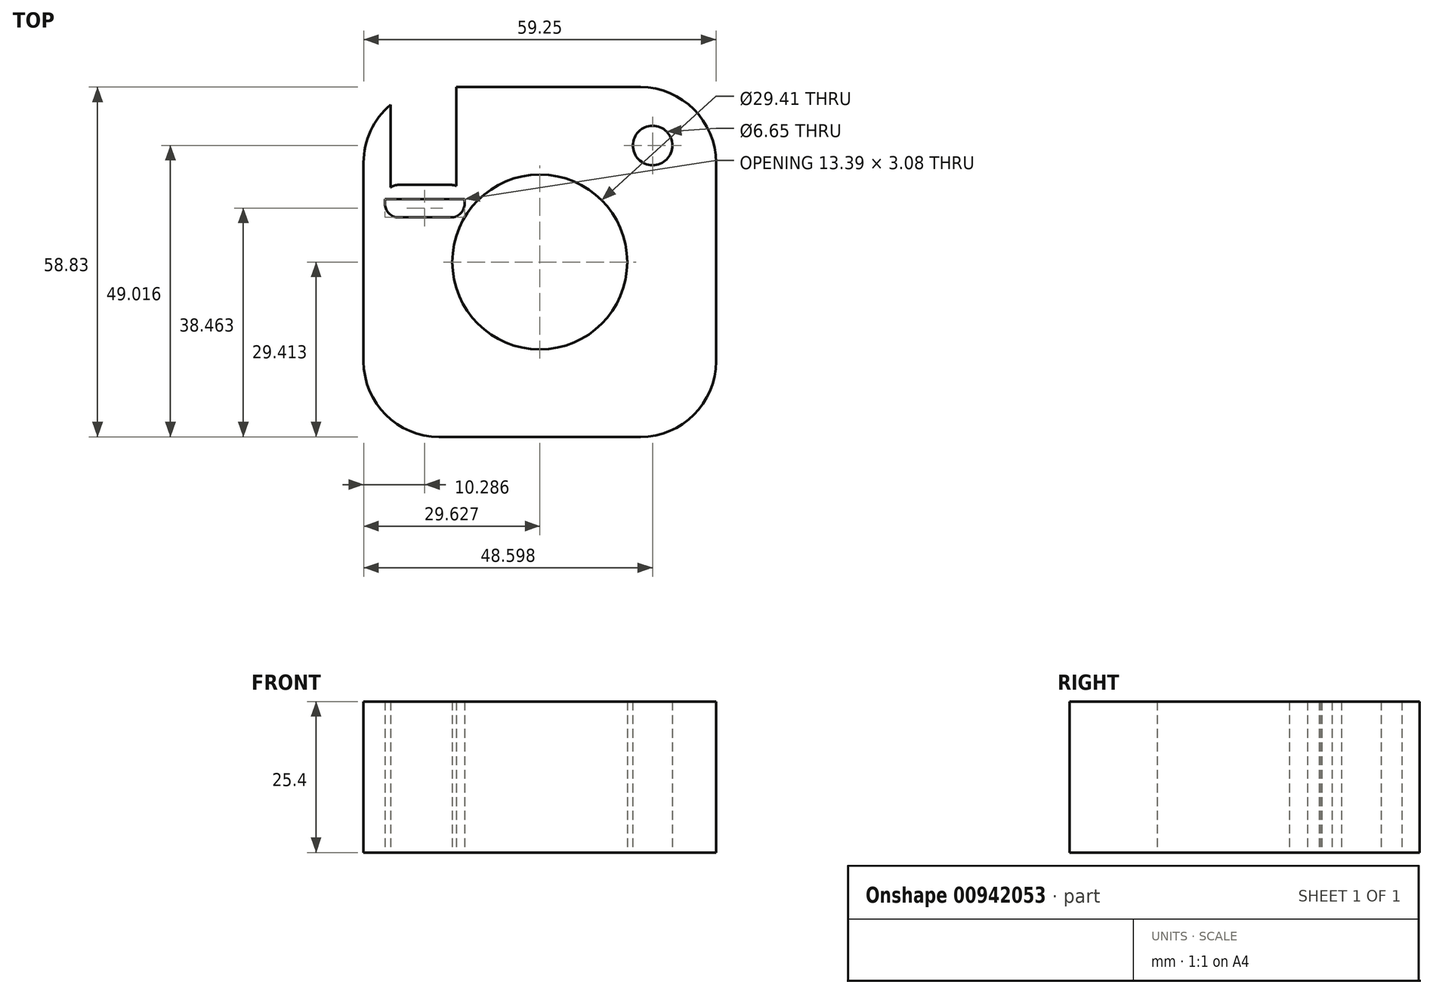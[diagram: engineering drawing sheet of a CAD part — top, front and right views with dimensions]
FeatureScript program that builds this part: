
annotation { "Feature Type Name" : "Feature", "Feature Type Description" : "" }
export const myFeature = defineFeature(function(context is Context, id is Id, definition is map)
    precondition{}
    {
        {
            var Q0;
            Q0=qCreatedBy(makeId("Top.planeOp"),FACE);
            var sketch = newSketch(context, id + "F0", { "sketchPlane" : qUnion([Q0])});
            skLineSegment(sketch, "E0.bottom", {"start": v(53.96, -66.45) * mm, "end": v(20.1, -66.45) * mm});
            skLineSegment(sketch, "E0.top", {"start": v(53.96, -7.62) * mm, "end": v(20.1, -7.62) * mm});
            skLineSegment(sketch, "E0.left", {"start": v(66.66, -53.75) * mm, "end": v(66.66, -20.32) * mm});
            skLineSegment(sketch, "E0.right", {"start": v(7.4, -53.75) * mm, "end": v(7.4, -20.32) * mm});
            skPoint(sketch, "E0.middle", {"position": v(37.04, -37.04) * mm});
            skPoint(sketch, "E0.middle.positionSnap0", {"position": v(37.04, 0) * mm});
            skPoint(sketch, "E0.middle.positionSnap1", {"position": v(0, -37.04) * mm});
            skPoint(sketch, "E0.centerSnap0", {"position": v(37.04, 0) * mm});
            skPoint(sketch, "E0.centerSnap1", {"position": v(0, -37.04) * mm});
            skPoint(sketch, "E1.visualSharp", {"position": v(7.4, -7.62) * mm});
            skArc(sketch, "E1.filletArc", {"start": v(20.1, -7.62) * mm, "mid": v(11.13, -11.34) * mm, "end": v(7.4, -20.32) * mm});
            skPoint(sketch, "E2.visualSharp", {"position": v(66.66, -7.62) * mm});
            skArc(sketch, "E2.filletArc", {"start": v(66.66, -20.32) * mm, "mid": v(62.94, -11.34) * mm, "end": v(53.96, -7.62) * mm});
            skPoint(sketch, "E3.visualSharp", {"position": v(66.66, -66.45) * mm});
            skArc(sketch, "E3.filletArc", {"start": v(53.96, -66.45) * mm, "mid": v(62.94, -62.73) * mm, "end": v(66.66, -53.75) * mm});
            skPoint(sketch, "E4.visualSharp", {"position": v(7.4, -66.45) * mm});
            skArc(sketch, "E4.filletArc", {"start": v(7.4, -53.75) * mm, "mid": v(11.13, -62.73) * mm, "end": v(20.1, -66.45) * mm});
            skCircle(sketch, "E5", {"center": v(37.04, -37.04) * mm, "radius": 14.7 * mm});
            skCircle(sketch, "E6", {"center": v(37.04, -37.04) * mm, "radius": 13.56 * mm});
            skCircle(sketch, "E7", {"center": v(37.04, -37.04) * mm, "radius": 10 * mm});
            skCircle(sketch, "E8", {"center": v(37.04, -37.04) * mm, "radius": 7.03 * mm});
            skLineSegment(sketch, "E9", {"start": v(7.4, -26.45) * mm, "end": v(66.66, -26.45) * mm});
            skLineSegment(sketch, "E10.bottom", {"start": v(22.1, -29.53) * mm, "end": v(13.28, -29.53) * mm});
            skLineSegment(sketch, "E10.top", {"start": v(22.1, -24.07) * mm, "end": v(13.28, -24.07) * mm});
            skLineSegment(sketch, "E10.left", {"start": v(24.4, -27.24) * mm, "end": v(24.4, -26.35) * mm});
            skLineSegment(sketch, "E10.right", {"start": v(11, -27.24) * mm, "end": v(11, -26.35) * mm});
            skPoint(sketch, "E10.middle", {"position": v(17.7, -26.8) * mm});
            skPoint(sketch, "E11.visualSharp", {"position": v(11, -29.53) * mm});
            skArc(sketch, "E11.filletArc", {"start": v(11, -27.24) * mm, "mid": v(11.67, -28.86) * mm, "end": v(13.28, -29.53) * mm});
            skPoint(sketch, "E12.visualSharp", {"position": v(24.4, -29.53) * mm});
            skArc(sketch, "E12.filletArc", {"start": v(22.1, -29.53) * mm, "mid": v(23.72, -28.86) * mm, "end": v(24.4, -27.24) * mm});
            skPoint(sketch, "E13.visualSharp", {"position": v(24.4, -24.07) * mm});
            skArc(sketch, "E13.filletArc", {"start": v(24.4, -26.35) * mm, "mid": v(23.72, -24.74) * mm, "end": v(22.1, -24.07) * mm});
            skPoint(sketch, "E14.visualSharp", {"position": v(11, -24.07) * mm});
            skArc(sketch, "E14.filletArc", {"start": v(13.28, -24.07) * mm, "mid": v(11.67, -24.74) * mm, "end": v(11, -26.35) * mm});
            skLineSegment(sketch, "E15", {"start": v(22.98, -7.62) * mm, "end": v(22.98, -24.24) * mm});
            skLineSegment(sketch, "E16", {"start": v(20.1, -7.62) * mm, "end": v(20.1, -24.07) * mm});
            skLineSegment(sketch, "E17", {"start": v(17.7, -24.07) * mm, "end": v(17.7, -7.85) * mm});
            skLineSegment(sketch, "E18", {"start": v(14.85, -24.07) * mm, "end": v(14.85, -8.76) * mm});
            skLineSegment(sketch, "E19", {"start": v(11.93, -24.51) * mm, "end": v(11.93, -10.6) * mm});
            skCircle(sketch, "E20", {"center": v(56, -17.43) * mm, "radius": 3.32 * mm});
            skCircle(sketch, "E21", {"center": v(56, -17.43) * mm, "radius": 1.92 * mm});
            skLineSegment(sketch, "E22", {"start": v(50.29, -11.85) * mm, "end": v(50.29, -22.49) * mm});
            skLineSegment(sketch, "E23", {"start": v(50.29, -22.49) * mm, "end": v(61.33, -22.49) * mm});
            skLineSegment(sketch, "E24", {"start": v(61.33, -22.49) * mm, "end": v(61.33, -11.98) * mm});
            skLineSegment(sketch, "E25", {"start": v(61.33, -11.98) * mm, "end": v(50.29, -11.85) * mm});
            skSolve(sketch);
        }
        {
            var Q0;
            {var subQ5=sQuery(id+"F0.wireOp",EDGE,"E19");Q0=makeQuery(id+"F0.imprint","IMPRINT",FACE,{"disambiguationData":[TD([[makeQuery(id+"F0.imprint","IMPRINT",EDGE,{"derivedFrom":subQ5}),1.0]])]});}
            var Q1;
            Q1=makeQuery(id+"F0.imprint","IMPRINT",FACE,{"disambiguationData":[TD([[makeQuery(id+"F0.imprint","IMPRINT",EDGE,{"derivedFrom":sQuery(id+"F0.wireOp",EDGE,"E0.bottom")}),-1.0]])]});
            var Q2;
            {var subQ9=sQuery(id+"F0.wireOp",EDGE,"E2.filletArc");Q2=makeQuery(id+"F0.imprint","IMPRINT",FACE,{"disambiguationData":[TD([[makeQuery(id+"F0.imprint","IMPRINT",EDGE,{"derivedFrom":subQ9}),1.0]])]});}
            var Q3;
            {var subQ5=sQuery(id+"F0.wireOp",EDGE,"E10.right");var subQ7=sQuery(id+"F0.wireOp",EDGE,"E9");var subQ8=makeQuery(id+"F0.imprint","INTERSECT",VERTEX,{"derivedFrom":[subQ7,subQ5]});Q3=makeQuery(id+"F0.imprint","IMPRINT",FACE,{"disambiguationData":[TD([[makeQuery(id+"F0.imprint","IMPRINT",EDGE,{"disambiguationData":[TD([[subQ8,-1.0]])],"derivedFrom":subQ7}),1.0]])]});}
            var Q4;
            Q4=makeQuery(id+"F0.imprint","IMPRINT",FACE,{"disambiguationData":[TD([[makeQuery(id+"F0.imprint","IMPRINT",EDGE,{"derivedFrom":sQuery(id+"F0.wireOp",EDGE,"E20")}),-1.0]])]});
            extrude(context, id + "F1", {"entities" : qUnion([Q0, Q1, Q2, Q3, Q4]), "depth" : 25.4 * mm, "offsetDistance" : 25.4 * mm});
        }
    });
